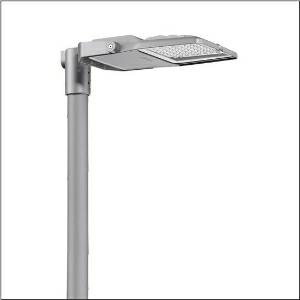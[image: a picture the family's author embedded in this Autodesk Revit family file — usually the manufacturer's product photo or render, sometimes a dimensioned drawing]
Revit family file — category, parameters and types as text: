
# Revit family: floodlight_fl_21_mini___pl64_5xa7776b2e3a_216f
name_source: partatom
category: Lighting Fixtures
units: mm (PartAtom-declared; Revit-internal decimal feet)

## family parameters
Cut with Voids When Loaded = No
Host = Face
Light Source = No
Part Type = Normal
Room Calculation Point = No
Round Connector Dimension = Use Diameter
Shared = No

## types (1)
- --- (1 x LED, 6010 lm, 45.7 W, 3000K)
    Apparent Load = 46 VA
    CIE Flux Codes = 28 80 98 100 100
    Color Rendering = 70
    Color Temperature = 3000K
    Default Elevation = 1800 mm
    Description = Floodlight FL 21 mini, floodlight, primary light control with lens, of PMMA, primary optical cover: protective disc, of toughened safety glass, transparent, light distribution: PL64, light emission: direct distribution, installation type: surface-mounted, LED, High Power LED, rated luminous flux: 6.010lm, luminous efficacy: 132lm/W, light colour: 730, colour temperature: 3000K, control gear: Smart Interface (Zhaga), control: flexible luminous flux parameterisation, time-dependent luminous flux control, constant luminous flux control, overheat protection, pre-setting: logarithmic dimming characteristic, with terminal, 6-pole, mains connection: 220..240V, AC, 50/60Hz, start of lifetime: 46W, end of service life: 48W, reduction: 22W, luminaire housing, of diecast aluminium, powder-coated, Siteco® metallic grey (DB 702S), corrosivity category C5 mid according to DIN EN ISO 12944, suitable for swimming pools, chlorine-resistant, sealing non-destructively replaceable, please order mast flange separately, mast bracket, of steel, galvanised, powder-coated, Siteco® metallic grey (DB 702S), Smart Interface below and above, protection rating (complete): IP66, insulation class (complete): insulation class II (safety insulation), certification: CE, ENEC, VDE, protection symbol: D, impact resistance: IK08, permissible operating ambient temperature: -40..+40°C, permissible operating ambient temperature for outdoor applications: -40..+50°C, standard: DIN EN 12944, LABS conformity tested according to VDMA 24364:2018-05, packaging unit: 1 piece

Light Distribution: PL64
    Height = 70 mm
    Lamp = 1 x LED
    Lamp Light Flux = 6010 lm
    Lamp Power = 45.7 W
    Lamp count = 1
    Length = 485 mm
    Luminous efficacy = 132 lm/W
    Manufacturer = Siteco
    ModVariant = No
    Model = 5XA7776B2E3A
    Number of Poles = 1
    OnlyDefault = Yes
    Power Factor = 1
    Product Name = Floodlight FL 21 mini | PL64
    Product group = floodlight | pylon annexe
    ProductGroupID = 6200
    Protection Class = Protection class II
    Protection Degree = IP 66
    RLX_Detail_Level = 1
    RLX_Emergency_Light_Flux = 0 lm
    RLX_Emergency_Type = 0
    RLX_Emergency_Type_DB = No
    RlxData = <blob elided: 101041 chars, md5=2119a975>
    Socket = socket
    Standby Power = 0 W
    System Light Flux = 6010 lm
    System Power = 46 W
    Type Comments = factory setting: luminous flux: 100 % | dim-lin: 254 | 463 mA
    Type Image = l_1007125.jpg
    URL = http://relux.com
    VarID = @adj_165476
    Voltage = 0 V
    Weight = 0.00 kg
    Width = 337 mm

## geometry (parser evidence)
native form markers: Blend x4, Sweep x13
no freeform markers — native parametric forms only
